# Revit family: BDG_BossDesign_MEWS_MWS_OP
name_source: partatom
category: Furniture
revit_build: Autodesk Revit 2018 (Build: 20190510_1515(x64)
units: mm (PartAtom-declared; Revit-internal decimal feet)

## family parameters
Always vertical = Yes
Cut with Voids When Loaded = No
Room Calculation Point = No
Shared = Yes
Work Plane-Based = No

## types (1)
- Mews_OP POD
    BIMObjectName = BDG_BossDesign_Mews_OP_POD
    Description = Mews
    Features = Powder coated frame
    FloorMaterial = BDG_Camira_Fabric_Lucia-SombreroYB046
    ManufacturerName = Boss Design
    ManufacturerURL = www.bossdesign.com
    Material = Glass
    Model = Mews_OP-POD
    ModelNumber = Mews_OP-POD
    ModelReference = Mews
    Name = Mews_BossDesign
    Nominal Depth = 1265 mm
    Nominal Height = 2225 mm
    Nominal Width = 2430 mm
    ProductInformation = https://www.bossdesign.com
    Shape = Rectangular
    Size = 1265 x 2430 x 2225mm
    URL = www.bossdesign.com
    Version = 1

## geometry (parser evidence)
native form markers: Blend x4, Sweep x18
no freeform markers — native parametric forms only
